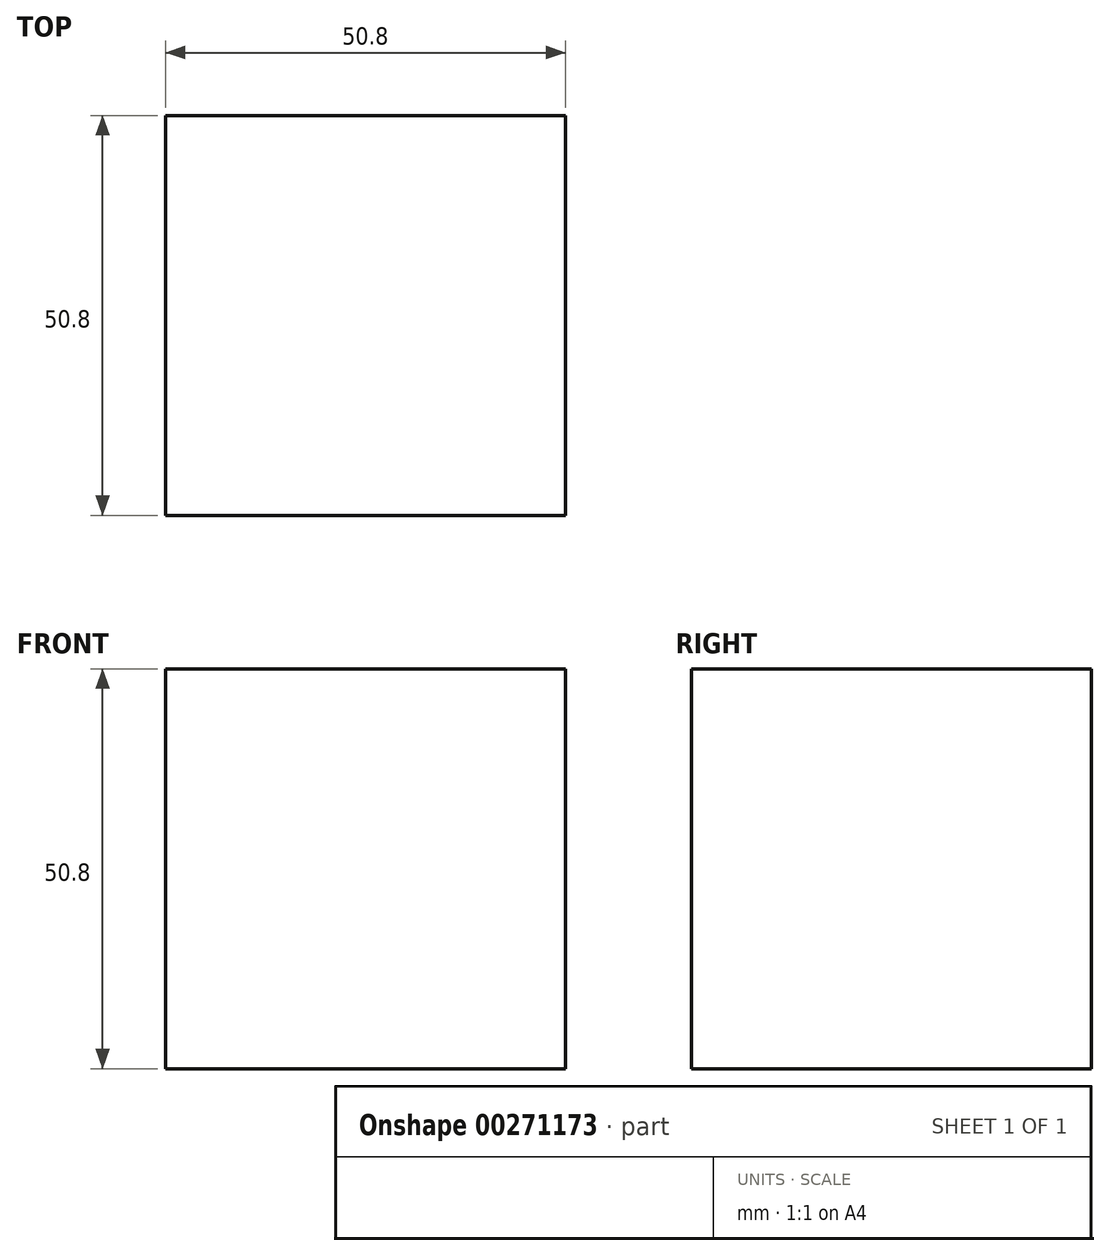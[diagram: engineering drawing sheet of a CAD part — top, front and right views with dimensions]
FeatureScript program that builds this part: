
annotation { "Feature Type Name" : "Feature", "Feature Type Description" : "" }
export const myFeature = defineFeature(function(context is Context, id is Id, definition is map)
    precondition{}
    {
        {
            var Q0;
            Q0=qCreatedBy(makeId("Front.planeOp"),FACE);
            var sketch = newSketch(context, id + "F0", { "sketchPlane" : qUnion([Q0])});
            skLineSegment(sketch, "E0.bottom", {"start": v(0, 0) * mm, "end": v(-50.8, 0) * mm});
            skLineSegment(sketch, "E0.top", {"start": v(0, 50.8) * mm, "end": v(-50.8, 50.8) * mm});
            skLineSegment(sketch, "E0.left", {"start": v(0, 0) * mm, "end": v(0, 50.8) * mm});
            skLineSegment(sketch, "E0.right", {"start": v(-50.8, 0) * mm, "end": v(-50.8, 50.8) * mm});
            skSolve(sketch);
        }
        {
            var Q0;
            Q0 = qSketchRegion(id + "F0", true);
            extrude(context, id + "F1", {"entities" : qUnion([Q0]), "depth" : 50.8 * mm});
        }
    });
